# Revit family: LC3535
name_source: partatom
category: Luminarias
units: mm (PartAtom-declared; Revit-internal decimal feet)

## family parameters
Compartido = Sí
Corte con vacíos al cargar = No
Cota de conector redondo = Diámetro de uso
Origen de luz = No
Punto de cálculo de habitación = No
Se basa en plano de trabajo = Sí
Siempre vertical = No
Tipo de pieza = Normal

## types (1)
- PERFILES_LC3535
    Descripción = PERFIL DE ALUMINIO CON DIFUSOR LECHOSO PARA ALOJAR TIRA LUMINOSA DE HASTA 31MM DE ANCHO. INSTALACION SOBRE SUPERFICIES PLANAS O COMO EMPOTRADO, IDEAL PARA ATENUAR EL BRILLO E INCORPORAR LA LUZ AL AMBIENTE. PRESENTACION DE 2 METROS. REQUEIRE ACCESORIOS COMO TAPA FINAL PARA EXTREMOS.
    Elevación por defecto = 1219 mm
    Fabricante = BRILLANT
    Longitud = 2000 mm  [stored 6.56168 ft]
    Modelo = LC3535
    Tapa Final 3535.1 = 1

note: [stored X ft] marks values corroborated as IEEE doubles in the binary element streams (Revit-internal decimal feet)

## geometry (parser evidence)
native form markers: Blend x2
no freeform markers — native parametric forms only
